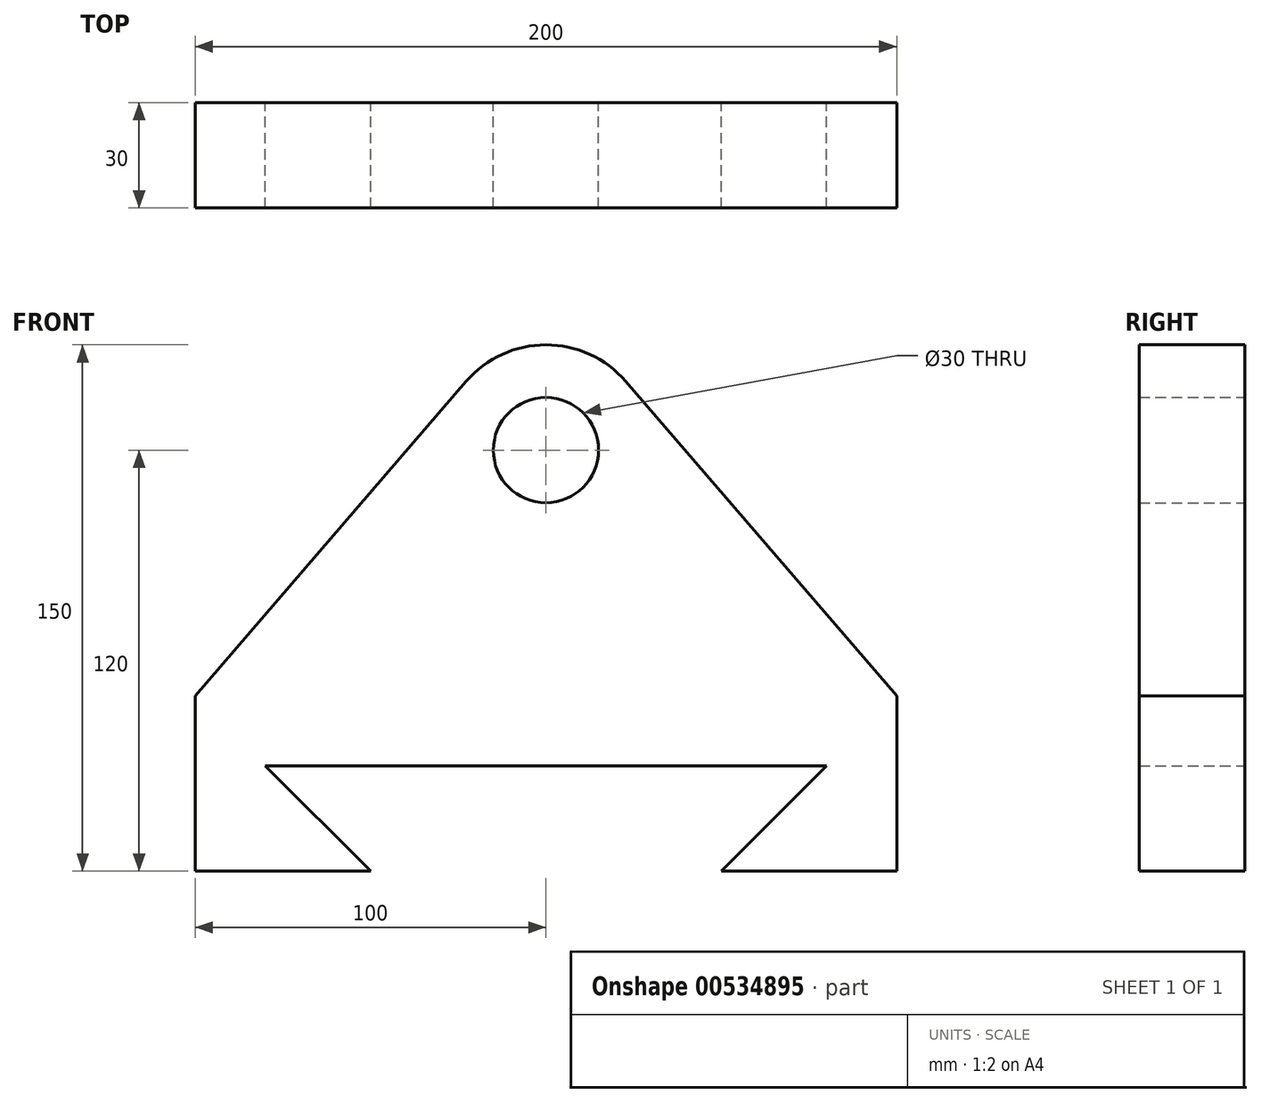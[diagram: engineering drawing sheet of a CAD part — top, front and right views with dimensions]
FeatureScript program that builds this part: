
annotation { "Feature Type Name" : "Feature", "Feature Type Description" : "" }
export const myFeature = defineFeature(function(context is Context, id is Id, definition is map)
    precondition{}
    {
        {
            var Q0;
            Q0=qCreatedBy(makeId("Front.planeOp"),FACE);
            var sketch = newSketch(context, id + "F0", { "sketchPlane" : qUnion([Q0])});
            skCircle(sketch, "E0", {"center": v(0, 0) * mm, "radius": 15 * mm});
            skCircle(sketch, "E1", {"center": v(0, 0) * mm, "radius": 30 * mm});
            skLineSegment(sketch, "E2", {"start": v(-100, -70) * mm, "end": v(100, -70) * mm});
            skLineSegment(sketch, "E3", {"start": v(-100, -70) * mm, "end": v(-22.72, 19.6) * mm});
            skLineSegment(sketch, "E4", {"start": v(22.72, 19.6) * mm, "end": v(100, -70) * mm});
            skLineSegment(sketch, "E5", {"start": v(0, 0) * mm, "end": v(0, -70) * mm, "construction": true});
            skLineSegment(sketch, "E6", {"start": v(-100, -70) * mm, "end": v(-100, -120) * mm});
            skLineSegment(sketch, "E7", {"start": v(-100, -120) * mm, "end": v(-50, -120) * mm});
            skLineSegment(sketch, "E8", {"start": v(-50, -120) * mm, "end": v(-80, -90) * mm});
            skLineSegment(sketch, "E9", {"start": v(-80, -90) * mm, "end": v(80, -90) * mm});
            skLineSegment(sketch, "E10", {"start": v(80, -90) * mm, "end": v(50, -120) * mm});
            skLineSegment(sketch, "E11", {"start": v(50, -120) * mm, "end": v(100, -120) * mm});
            skLineSegment(sketch, "E12", {"start": v(100, -120) * mm, "end": v(100, -70) * mm});
            skLineSegment(sketch, "E13", {"start": v(0, -70) * mm, "end": v(0, -90) * mm, "construction": true});
            skSolve(sketch);
        }
        {
            var Q0;
            Q0 = qSketchRegion(id + "F0", true);
            extrude(context, id + "F1", {"entities" : qUnion([Q0]), "depth" : 30 * mm, "offsetDistance" : 25 * mm});
        }
    });
